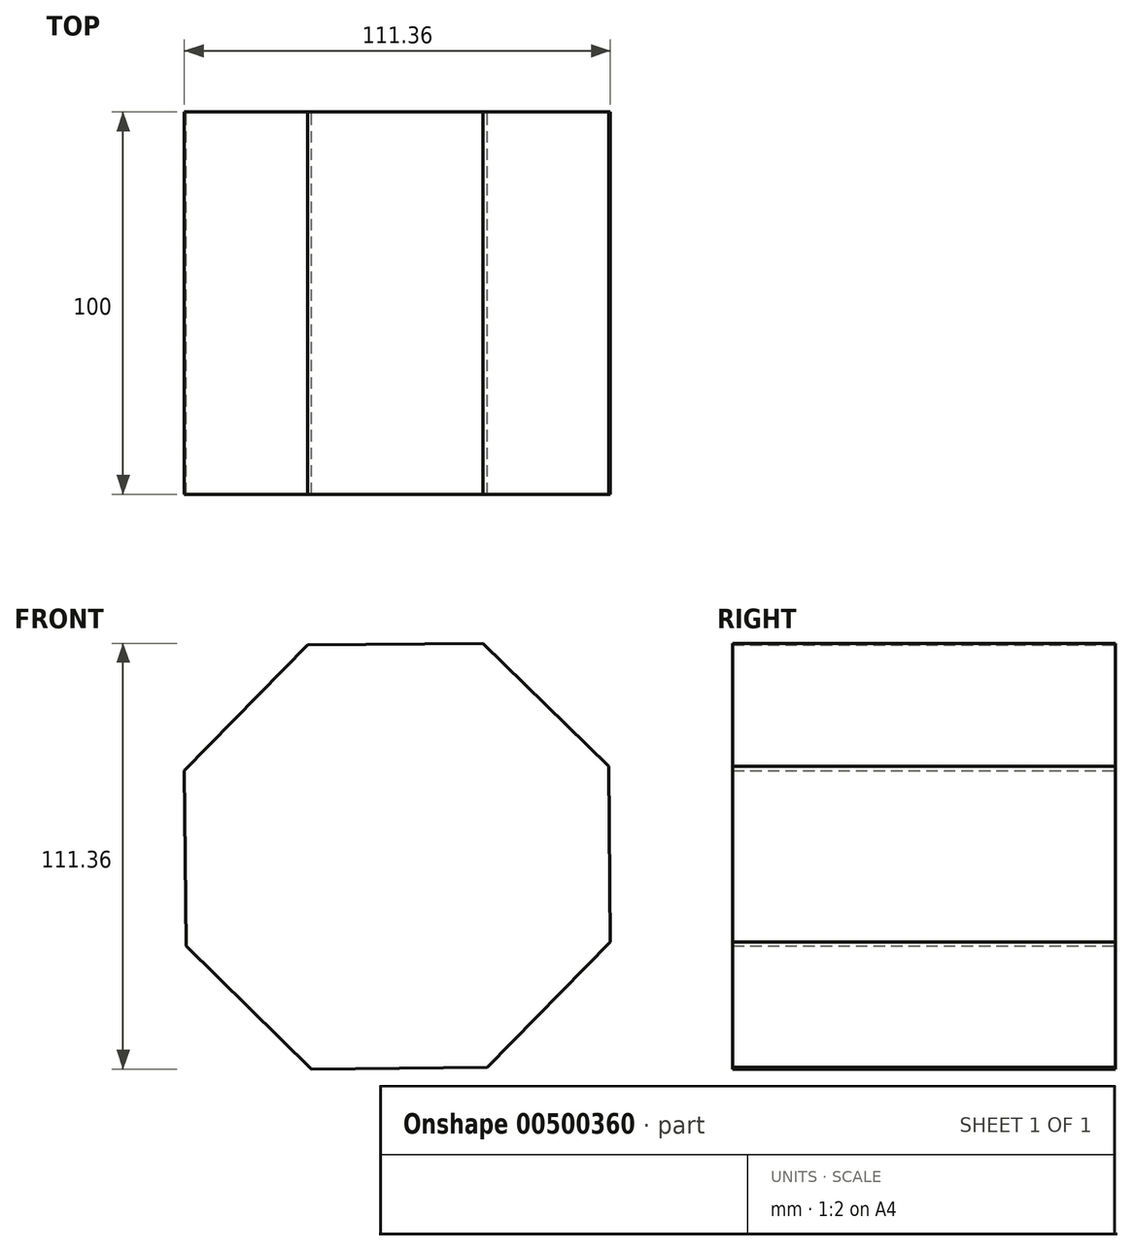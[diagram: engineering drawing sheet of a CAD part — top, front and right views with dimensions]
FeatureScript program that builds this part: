
annotation { "Feature Type Name" : "Feature", "Feature Type Description" : "" }
export const myFeature = defineFeature(function(context is Context, id is Id, definition is map)
    precondition{}
    {
        {
            var Q0;
            Q0=qCreatedBy(makeId("Front.planeOp"),FACE);
            var sketch = newSketch(context, id + "F0", { "sketchPlane" : qUnion([Q0])});
            skCircle(sketch, "E0.cCircle", {"center": v(0, 0) * mm, "radius": 55.46 * mm, "construction": true});
            skLineSegment(sketch, "E0.0", {"start": v(22.42, 55.68) * mm, "end": v(55.23, 23.52) * mm});
            skLineSegment(sketch, "E0.1", {"start": v(55.23, 23.52) * mm, "end": v(55.68, -22.42) * mm});
            skLineSegment(sketch, "E0.2", {"start": v(55.68, -22.42) * mm, "end": v(23.52, -55.23) * mm});
            skLineSegment(sketch, "E0.3", {"start": v(23.52, -55.23) * mm, "end": v(-22.42, -55.68) * mm});
            skLineSegment(sketch, "E0.4", {"start": v(-22.42, -55.68) * mm, "end": v(-55.23, -23.52) * mm});
            skLineSegment(sketch, "E0.5", {"start": v(-55.23, -23.52) * mm, "end": v(-55.68, 22.42) * mm});
            skLineSegment(sketch, "E0.6", {"start": v(-55.68, 22.42) * mm, "end": v(-23.52, 55.23) * mm});
            skLineSegment(sketch, "E0.7", {"start": v(-23.52, 55.23) * mm, "end": v(22.42, 55.68) * mm});
            skPoint(sketch, "E0.0.midPoint", {"position": v(38.83, 39.6) * mm});
            skSolve(sketch);
        }
        {
            var Q0;
            Q0 = qSketchRegion(id + "F0", true);
            extrude(context, id + "F1", {"entities" : qUnion([Q0]), "depth" : 100 * mm});
        }
    });
